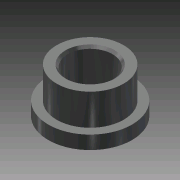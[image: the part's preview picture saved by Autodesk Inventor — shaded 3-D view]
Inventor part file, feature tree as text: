
AUTODESK INVENTOR PART (.ipt)
format: ipt  version: 2011 (Build 150239000, 239)  size: 98,304 bytes
history: native  units: in
note: dims shown in document units (in); Inventor stores cm internally (conversion verified against a paired STEP export)
features: revolve x1, chamfer x1, fillet x1, sketch x1
ambient origin geometry x8: Origin, YZ Plane, XZ Plane, XY Plane, X Axis, Y Axis, Z Axis, Center Point
bodies: Solid1 (feature_tree)
feature tree (4):
  revolve  "Revolution1"  [1 undecoded]
  chamfer  "Chamfer1"  Distance=0.375in
  fillet  "Fillet1"  Radius=0.25in
  sketch  "Sketch1"  dims[d0=0.5in d1=0.469in d2=0.375in d3=0.25in d4=0.15in d5=90.0deg d6=0.025in d7=0.125in d8=45.0deg d9=0.005in]
note: 1 required parameter value undecoded (feature->parameter linkage not recoverable at this tier; creation-order binding heuristic only, values carry confidence <= 0.55)
